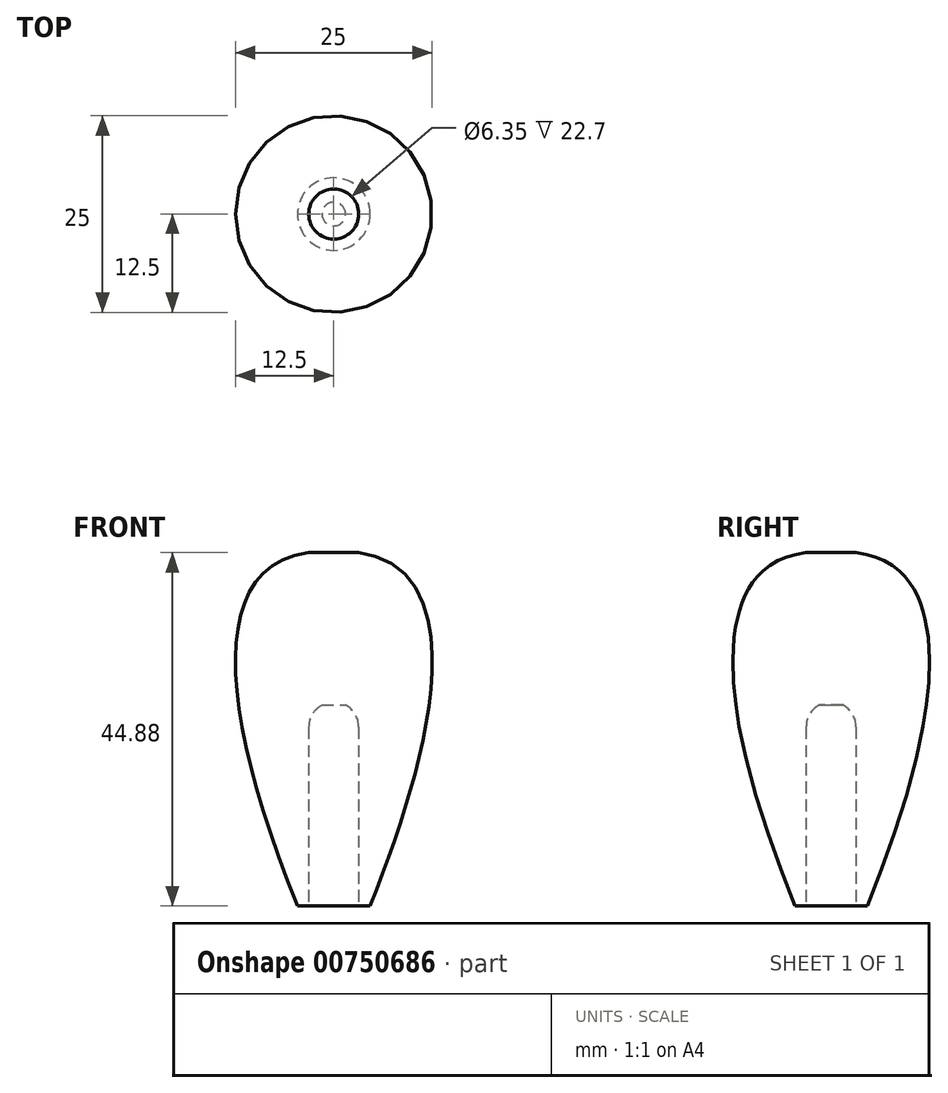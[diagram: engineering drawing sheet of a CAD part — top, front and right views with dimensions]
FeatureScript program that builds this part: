
annotation { "Feature Type Name" : "Feature", "Feature Type Description" : "" }
export const myFeature = defineFeature(function(context is Context, id is Id, definition is map)
    precondition{}
    {
        {
            var Q0;
            Q0=qCreatedBy(makeId("Front.planeOp"),FACE);
            var sketch = newSketch(context, id + "F0", { "sketchPlane" : qUnion([Q0])});
            skLineSegment(sketch, "E0", {"start": v(0, 0) * mm, "end": v(0, 45) * mm, "construction": true});
            skLineSegment(sketch, "E1", {"start": v(0, 0) * mm, "end": v(4.61, 0) * mm, "construction": true});
            skLineSegment(sketch, "E2", {"start": v(0, 22.7) * mm, "end": v(0, 45) * mm});
            skFitSpline(sketch, "E3", {"points": [v(0, 45) * mm, v(11.73, 37.24) * mm, v(4.61, 0) * mm], "startDerivative": vector(56.23, 2.4) * mm, "endDerivative": vector(-31.66, -78.98) * mm});
            skLineSegment(sketch, "E4", {"start": v(12.5, 30.96) * mm, "end": v(12.5, 2.78) * mm, "construction": true});
            skLineSegment(sketch, "E5", {"start": v(4.61, 0) * mm, "end": v(4.61, 0) * mm});
            skLineSegment(sketch, "E6", {"start": v(3.17, 22.7) * mm, "end": v(3.17, 0) * mm});
            skLineSegment(sketch, "E7", {"start": v(4.61, 0) * mm, "end": v(3.18, 0) * mm});
            skLineSegment(sketch, "E8", {"start": v(0, 25.5) * mm, "end": v(1.5, 25.5) * mm});
            skArc(sketch, "E9", {"start": v(1.5, 25.5) * mm, "mid": v(2.72, 24.33) * mm, "end": v(3.17, 22.7) * mm});
            skLineSegment(sketch, "E10", {"start": v(3.17, 22.7) * mm, "end": v(0, 22.7) * mm, "construction": true});
            skLineSegment(sketch, "E11", {"start": v(0, 44.88) * mm, "end": v(3.17, 44.88) * mm});
            skSolve(sketch);
        }
        {
            var Q0;
            Q0=makeQuery(id+"F0.imprint","IMPRINT",FACE,{"disambiguationData":[TD([[makeQuery(id+"F0.imprint","IMPRINT",EDGE,{"derivedFrom":sQuery(id+"F0.wireOp",EDGE,"E6")}),1.0]])]});
            var Q1;
            Q1=sQuery(id+"F0.wireOp",EDGE,"E2");
            revolve(context, id + "F1", {"surfaceOperationType" : NewSurfaceOperationType.NEW, "entities" : qUnion([Q0]), "axis" : qUnion([Q1]), "revolveType" : RevolveType.FULL});
        }
    });
